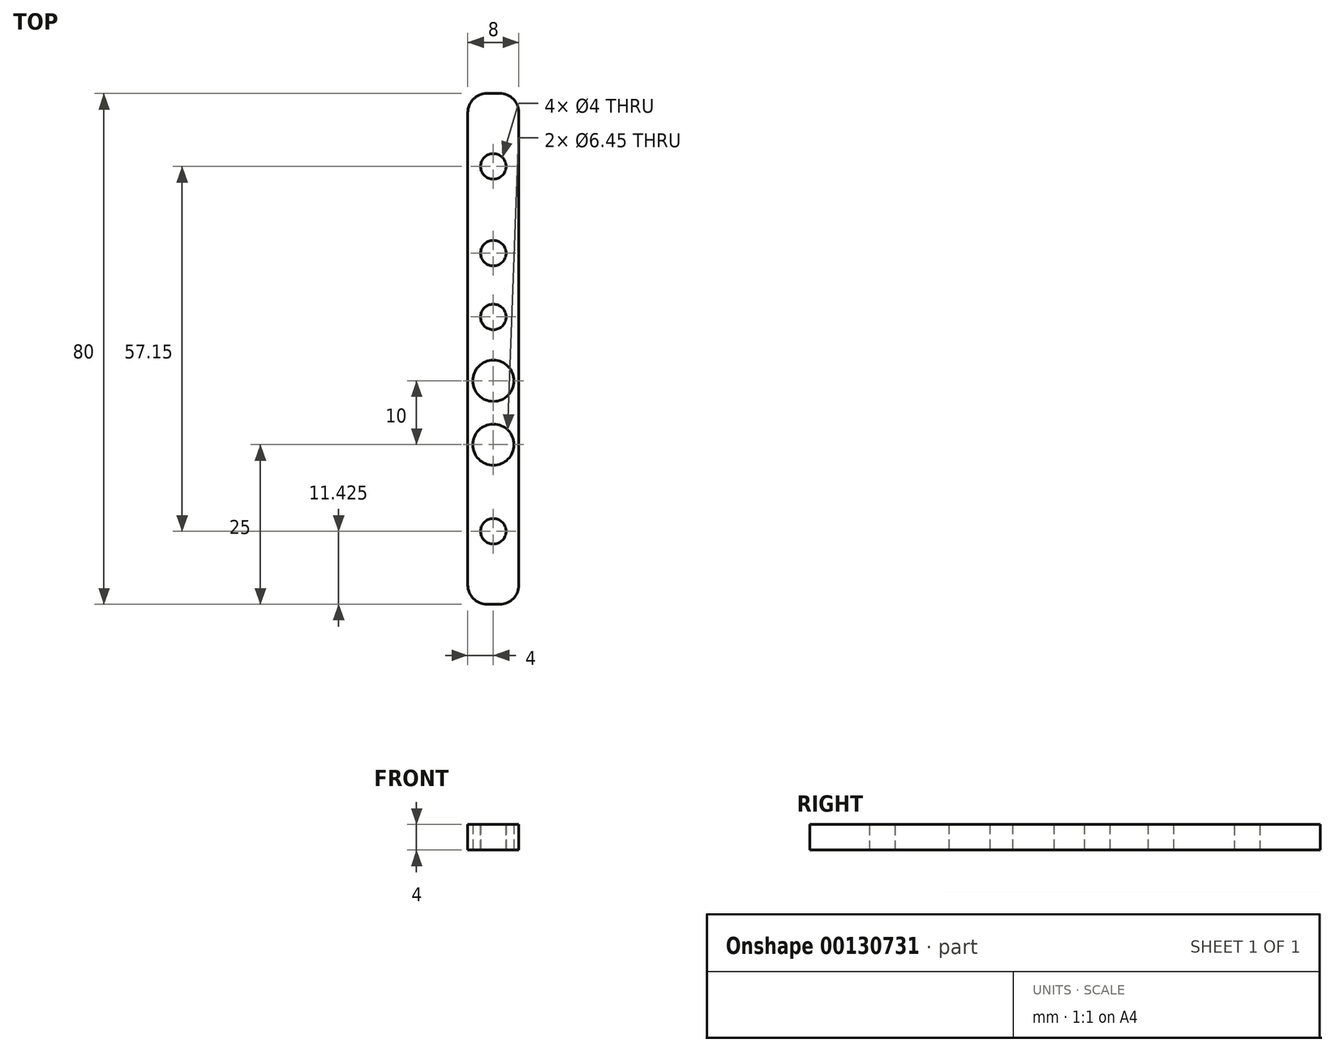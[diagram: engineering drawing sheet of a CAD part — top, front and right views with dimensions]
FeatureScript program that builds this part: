
annotation { "Feature Type Name" : "Feature", "Feature Type Description" : "" }
export const myFeature = defineFeature(function(context is Context, id is Id, definition is map)
    precondition{}
    {
        {
            var Q0;
            Q0=qCreatedBy(makeId("Top.planeOp"),FACE);
            var sketch = newSketch(context, id + "F0", { "sketchPlane" : qUnion([Q0])});
            skLineSegment(sketch, "E0.bottom", {"start": v(4, -40) * mm, "end": v(-4, -40) * mm});
            skLineSegment(sketch, "E0.top", {"start": v(4, 40) * mm, "end": v(-4, 40) * mm});
            skLineSegment(sketch, "E0.left", {"start": v(4, -40) * mm, "end": v(4, 40) * mm});
            skLineSegment(sketch, "E0.right", {"start": v(-4, -40) * mm, "end": v(-4, 40) * mm});
            skPoint(sketch, "E0.middle", {"position": v(0, 0) * mm});
            skPoint(sketch, "E1", {"position": v(0, 28.57) * mm});
            skPoint(sketch, "E2.MirrorP", {"position": v(0, -28.57) * mm});
            skCircle(sketch, "E3", {"center": v(0, 5) * mm, "radius": 3.23 * mm});
            skCircle(sketch, "E4.MirrorC", {"center": v(0, -5) * mm, "radius": 3.23 * mm});
            skCircle(sketch, "E5", {"center": v(0, 15) * mm, "radius": 3.23 * mm});
            skCircle(sketch, "E6.MirrorC", {"center": v(0, -15) * mm, "radius": 3.23 * mm});
            skSolve(sketch);
        }
        {
            var Q0;
            Q0=makeQuery(id+"F0.imprint","IMPRINT",FACE,{"disambiguationData":[TD([[makeQuery(id+"F0.imprint","IMPRINT",EDGE,{"derivedFrom":sQuery(id+"F0.wireOp",EDGE,"E0.bottom")}),-1.0]])]});
            var Q1;
            Q1=makeQuery(id+"F0.imprint","IMPRINT",FACE,{"disambiguationData":[TD([[makeQuery(id+"F0.imprint","IMPRINT",EDGE,{"derivedFrom":sQuery(id+"F0.wireOp",EDGE,"E3")}),1.0]])]});
            var Q2;
            Q2=makeQuery(id+"F0.imprint","IMPRINT",FACE,{"disambiguationData":[TD([[makeQuery(id+"F0.imprint","IMPRINT",EDGE,{"derivedFrom":sQuery(id+"F0.wireOp",EDGE,"E4.MirrorC")}),-1.0]])]});
            var Q3;
            Q3=makeQuery(id+"F0.imprint","IMPRINT",FACE,{"disambiguationData":[TD([[makeQuery(id+"F0.imprint","IMPRINT",EDGE,{"derivedFrom":sQuery(id+"F0.wireOp",EDGE,"E5")}),1.0]])]});
            var Q4;
            Q4=makeQuery(id+"F0.imprint","IMPRINT",FACE,{"disambiguationData":[TD([[makeQuery(id+"F0.imprint","IMPRINT",EDGE,{"derivedFrom":sQuery(id+"F0.wireOp",EDGE,"E6.MirrorC")}),-1.0]])]});
            extrude(context, id + "F1", {"entities" : qUnion([Q0, Q1, Q2, Q3, Q4]), "depth" : 10 * mm});
        }
        {
            var Q0;
            Q0=makeQuery(id+"F1.opExtrude","CAP_FACE",FACE,{"disambiguationData":[OSD([sQuery(id+"F0.wireOp",EDGE,"E0.bottom"),sQuery(id+"F0.wireOp",EDGE,"E0.top"),sQuery(id+"F0.wireOp",EDGE,"E0.left"),sQuery(id+"F0.wireOp",EDGE,"E0.right")])],"isStart":false});
            var sketch = newSketch(context, id + "F2", { "sketchPlane" : qUnion([Q0])});
            skPoint(sketch, "E7.0", {"position": v(0, 28.57) * mm});
            skPoint(sketch, "E7.1", {"position": v(0, -28.57) * mm});
            skCircle(sketch, "E8.0", {"center": v(0, -5) * mm, "radius": 3.23 * mm});
            skCircle(sketch, "E9.0", {"center": v(0, 5) * mm, "radius": 3.23 * mm});
            skCircle(sketch, "E10.0", {"center": v(0, 15) * mm, "radius": 3.23 * mm});
            skCircle(sketch, "E10.1", {"center": v(0, -15) * mm, "radius": 3.23 * mm});
            skSolve(sketch);
        }
        {
            var Q0;
            Q0=sQuery(id+"F2.wireOp",VERTEX,"E7.0");
            var Q1;
            Q1=sQuery(id+"F2.wireOp",VERTEX,"E7.1");
            var Q2;
            Q2=makeQuery(id+"F1.opExtrude","SWEPT_BODY",BODY,{"disambiguationData":[OSD([sQuery(id+"F0.wireOp",EDGE,"E0.bottom"),sQuery(id+"F0.wireOp",EDGE,"E0.top"),sQuery(id+"F0.wireOp",EDGE,"E0.left"),sQuery(id+"F0.wireOp",EDGE,"E0.right")])]});
            hole(context, id + "F3", {"style" : HoleStyle.C_BORE, "endStyle" : HoleEndStyle.THROUGH, "holeDiameter" : 4 * mm, "cBoreDiameter" : 7 * mm, "cBoreDepth" : 4 * mm, "startFromSketch" : true, "locations" : qUnion([Q0, Q1]), "scope" : qUnion([Q2]), "isTappedThrough" : true});
        }
        {
            var Q0;
            Q0=makeQuery(id+"F1.opExtrude","SWEPT_EDGE",EDGE,{"disambiguationData":[OSD([sQuery(id+"F0.wireOp",EDGE,"E0.top"),sQuery(id+"F0.wireOp",EDGE,"E0.right")])]});
            var Q1;
            Q1=makeQuery(id+"F1.opExtrude","SWEPT_EDGE",EDGE,{"disambiguationData":[OSD([sQuery(id+"F0.wireOp",EDGE,"E0.top"),sQuery(id+"F0.wireOp",EDGE,"E0.left")])]});
            var Q2;
            Q2=makeQuery(id+"F1.opExtrude","SWEPT_EDGE",EDGE,{"disambiguationData":[OSD([sQuery(id+"F0.wireOp",EDGE,"E0.bottom"),sQuery(id+"F0.wireOp",EDGE,"E0.right")])]});
            var Q3;
            Q3=makeQuery(id+"F1.opExtrude","SWEPT_EDGE",EDGE,{"disambiguationData":[OSD([sQuery(id+"F0.wireOp",EDGE,"E0.bottom"),sQuery(id+"F0.wireOp",EDGE,"E0.left")])]});
            fillet(context, id + "F4", {"entities" : qUnion([Q0, Q1, Q2, Q3]), "radius" : 3 * mm, "tangentPropagation" : true, "allowEdgeOverflow" : false});
        }
        {
            var Q0;
            Q0=makeQuery(id+"F2.imprint","IMPRINT",FACE,{"disambiguationData":[TD([[makeQuery(id+"F2.imprint","IMPRINT",EDGE,{"derivedFrom":sQuery(id+"F2.wireOp",EDGE,"E8.0")}),-1.0]])]});
            var Q1;
            Q1=makeQuery(id+"F2.imprint","IMPRINT",FACE,{"disambiguationData":[TD([[makeQuery(id+"F2.imprint","IMPRINT",EDGE,{"derivedFrom":sQuery(id+"F2.wireOp",EDGE,"E9.0")}),1.0]])]});
            var Q2;
            Q2=makeQuery(id+"F2.imprint","IMPRINT",FACE,{"disambiguationData":[TD([[makeQuery(id+"F2.imprint","IMPRINT",EDGE,{"derivedFrom":sQuery(id+"F2.wireOp",EDGE,"E10.0")}),1.0]])]});
            var Q3;
            Q3=makeQuery(id+"F2.imprint","IMPRINT",FACE,{"disambiguationData":[TD([[makeQuery(id+"F2.imprint","IMPRINT",EDGE,{"derivedFrom":sQuery(id+"F2.wireOp",EDGE,"E10.1")}),-1.0]])]});
            extrude(context, id + "F5", {"entities" : qUnion([Q0, Q1, Q2, Q3]), "operationType" : NewBodyOperationType.REMOVE, "oppositeDirection" : true, "depth" : 6 * mm});
        }
        {
            var Q0;
            Q0=sQuery(id+"F0.wireOp",VERTEX,"E5.center");
            var Q1;
            Q1=sQuery(id+"F0.wireOp",VERTEX,"E3.center");
            var Q2;
            Q2=sQuery(id+"F0.wireOp",VERTEX,"E4.MirrorC.center");
            var Q3;
            Q3=sQuery(id+"F0.wireOp",VERTEX,"E6.MirrorC.center");
            var Q4;
            Q4=makeQuery(id+"F1.opExtrude","SWEPT_BODY",BODY,{"disambiguationData":[OSD([sQuery(id+"F0.wireOp",EDGE,"E0.bottom"),sQuery(id+"F0.wireOp",EDGE,"E0.top"),sQuery(id+"F0.wireOp",EDGE,"E0.left"),sQuery(id+"F0.wireOp",EDGE,"E0.right")])]});
            hole(context, id + "F6", {"style" : HoleStyle.SIMPLE, "endStyle" : HoleEndStyle.THROUGH, "oppositeDirection" : true, "holeDiameter" : 4 * mm, "startFromSketch" : true, "locations" : qUnion([Q0, Q1, Q2, Q3]), "scope" : qUnion([Q4]), "isTappedThrough" : true});
        }
    });
